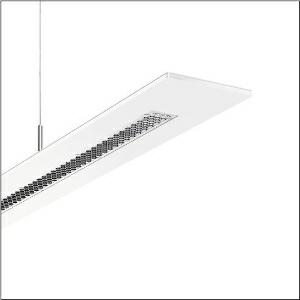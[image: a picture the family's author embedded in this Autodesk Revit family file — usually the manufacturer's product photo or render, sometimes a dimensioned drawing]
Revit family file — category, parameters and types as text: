
# Revit family: arktika_r__21_5mb2512l30840_559e
name_source: partatom
category: Lighting Fixtures
units: mm (PartAtom-declared; Revit-internal decimal feet)

## family parameters
Cut with Voids When Loaded = No
Host = Face
Light Source = No
Part Type = Normal
Room Calculation Point = No
Round Connector Dimension = Use Diameter
Shared = No

## types (1)
- Arktika® 21 (1 x LED 4000K / CRI = 80 (unbekannt), 4000 lm, 4000K)
    Apparent Load = 31 VA
    CIE Flux Codes = 81 100 100 79 100
    Color Rendering = 80
    Color Temperature = 4000K
    Default Elevation = 1800 mm
    Description = Arktika® 21, office luminaire, primary anti-glare with honeycomb louvre, of plastic, aluminium vaporised, highly specular, light emission: direct/indirect distribution, primary light characteristic: symmetric, installation type: suspended mounting, LED rated luminous flux: 4.000 lm, light colour: 840, colour temperature: 4000K, control gear: ECG, with terminal, 3-pole, mains connection: 220..240V, AC, 50/60Hz, rated input power: 31W, housing, of aluminium, powder-coated, traffic white (RAL 9016), 1-length, length: 1.250 mm, width: 120 mm, height: 8mm, protection rating (complete): IP20, insulation class (complete): insulation class II (safety insulation), certification: CE, packaging unit: 1 piece
    Height = 8 mm  [stored 0.0262467 ft]
    Lamp = 1 x LED 4000K / CRI >= 80 (unbekannt)
    Lamp Light Flux = 4000 lm
    Lamp count = 1
    Length = 1250 mm
    Luminous efficacy = 130 lm/W
    Manufacturer = Siteco
    ModVariant = No
    Model = 5MB2512L30840
    Mounting Place = Ceiling
    Mounting Type = Pendant
    Number of Poles = 1
    OnlyDefault = Yes
    Power Factor = 1
    Product Name = Arktika® 21
    Product group = office luminaire | ceiling pendant
    ProductGroupID = 905
    Protection Class = Protection class II
    Protection Degree = IP 20
    RLX_Detail_Level = 1
    RlxData = <blob elided: 36053 chars, md5=45c8607b>
    Socket = socket
    Standby Power = 0 W
    System Light Flux = 4000 lm
    System Power = 31 W
    Type Comments = Product without accessories
    Type Image = l_1006128.jpg
    URL = http://relux.com
    VarID = ---
    Voltage = 0 V
    Weight = 0.00 kg
    Width = 120 mm

note: [stored X ft] marks values corroborated as IEEE doubles in the binary element streams (Revit-internal decimal feet)

## geometry (parser evidence)
native form markers: Blend x4, Sweep x13
no freeform markers — native parametric forms only
